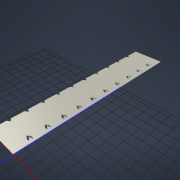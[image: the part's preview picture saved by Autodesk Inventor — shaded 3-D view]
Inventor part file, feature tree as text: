
AUTODESK INVENTOR PART (.ipt)
format: ipt  version: 2022 (Build 260153070, 153G)  size: 582,144 bytes
history: native  units: mm
features: extrude x1, sketch x1, other x1
ambient origin geometry x8: Origin, YZ Plane, XZ Plane, XY Plane, X Axis, Y Axis, Z Axis, Center Point
bodies: Body1 (feature_tree)
feature tree (3):
  extrude  "Выдавливание3"  Depth=145.0mm
  sketch  "Эскиз1"
  other  "Определение1"
